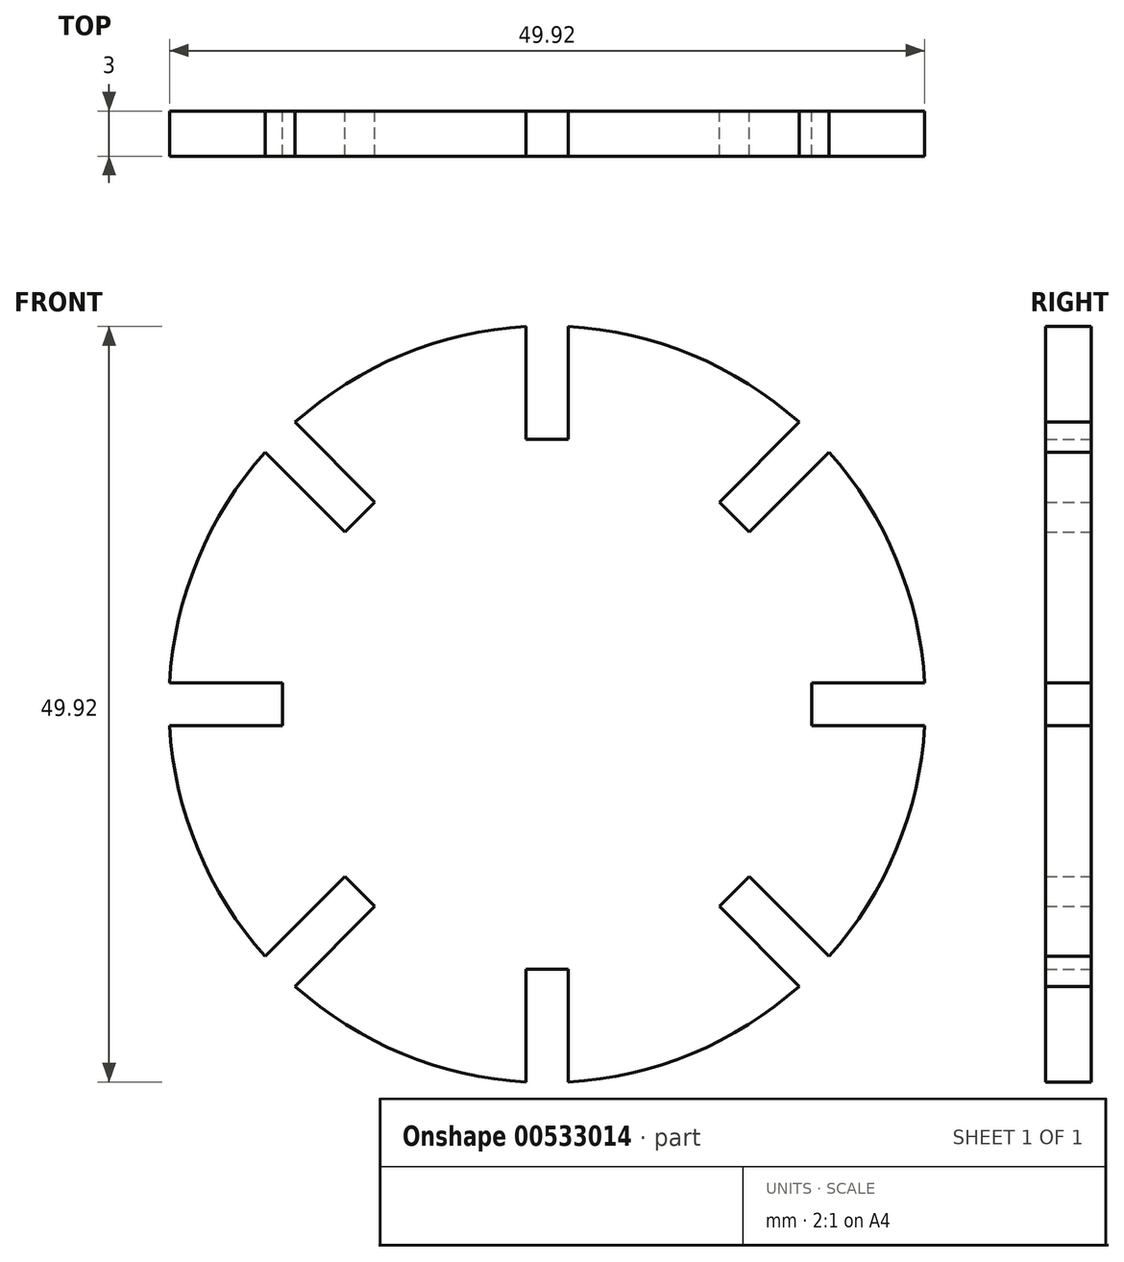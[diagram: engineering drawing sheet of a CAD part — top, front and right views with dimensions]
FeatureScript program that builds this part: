
annotation { "Feature Type Name" : "Feature", "Feature Type Description" : "" }
export const myFeature = defineFeature(function(context is Context, id is Id, definition is map)
    precondition{}
    {
        {
            var Q0;
            Q0=qCreatedBy(makeId("Front.planeOp"),FACE);
            var sketch = newSketch(context, id + "F0", { "sketchPlane" : qUnion([Q0])});
            skArc(sketch, "E0", {"start": v(16.66, 18.64) * mm, "mid": v(9.57, 23.1) * mm, "end": v(1.4, 24.96) * mm});
            skLineSegment(sketch, "E1.bottom", {"start": v(-1.4, 17.5) * mm, "end": v(1.4, 17.5) * mm});
            skLineSegment(sketch, "E1.left", {"start": v(-1.4, 17.5) * mm, "end": v(-1.4, 24.96) * mm});
            skLineSegment(sketch, "E1.right", {"start": v(1.4, 17.5) * mm, "end": v(1.4, 24.96) * mm});
            skPoint(sketch, "E1.middle", {"position": v(0, 25) * mm});
            skLineSegment(sketch, "E2.1.1", {"start": v(-11.38, 13.36) * mm, "end": v(-16.66, 18.64) * mm});
            skLineSegment(sketch, "E2.1.2", {"start": v(-13.36, 11.38) * mm, "end": v(-18.64, 16.66) * mm});
            skLineSegment(sketch, "E2.1.3", {"start": v(-13.36, 11.38) * mm, "end": v(-11.38, 13.36) * mm});
            skLineSegment(sketch, "E2.2.1", {"start": v(-17.5, 1.4) * mm, "end": v(-24.96, 1.4) * mm});
            skLineSegment(sketch, "E2.2.2", {"start": v(-17.5, -1.4) * mm, "end": v(-24.96, -1.4) * mm});
            skLineSegment(sketch, "E2.2.3", {"start": v(-17.5, -1.4) * mm, "end": v(-17.5, 1.4) * mm});
            skLineSegment(sketch, "E2.3.1", {"start": v(-13.36, -11.38) * mm, "end": v(-18.64, -16.66) * mm});
            skLineSegment(sketch, "E2.3.2", {"start": v(-11.38, -13.36) * mm, "end": v(-16.66, -18.64) * mm});
            skLineSegment(sketch, "E2.3.3", {"start": v(-11.38, -13.36) * mm, "end": v(-13.36, -11.38) * mm});
            skLineSegment(sketch, "E2.4.1", {"start": v(-1.4, -17.5) * mm, "end": v(-1.4, -24.96) * mm});
            skLineSegment(sketch, "E2.4.2", {"start": v(1.4, -17.5) * mm, "end": v(1.4, -24.96) * mm});
            skLineSegment(sketch, "E2.4.3", {"start": v(1.4, -17.5) * mm, "end": v(-1.4, -17.5) * mm});
            skLineSegment(sketch, "E2.5.1", {"start": v(11.38, -13.36) * mm, "end": v(16.66, -18.64) * mm});
            skLineSegment(sketch, "E2.5.2", {"start": v(13.36, -11.38) * mm, "end": v(18.64, -16.66) * mm});
            skLineSegment(sketch, "E2.5.3", {"start": v(13.36, -11.38) * mm, "end": v(11.38, -13.36) * mm});
            skLineSegment(sketch, "E2.6.1", {"start": v(17.5, -1.4) * mm, "end": v(24.96, -1.4) * mm});
            skLineSegment(sketch, "E2.6.2", {"start": v(17.5, 1.4) * mm, "end": v(24.96, 1.4) * mm});
            skLineSegment(sketch, "E2.6.3", {"start": v(17.5, 1.4) * mm, "end": v(17.5, -1.4) * mm});
            skLineSegment(sketch, "E2.7.1", {"start": v(13.36, 11.38) * mm, "end": v(18.64, 16.66) * mm});
            skLineSegment(sketch, "E2.7.2", {"start": v(11.38, 13.36) * mm, "end": v(16.66, 18.64) * mm});
            skLineSegment(sketch, "E2.7.3", {"start": v(11.38, 13.36) * mm, "end": v(13.36, 11.38) * mm});
            skPoint(sketch, "E3.orphan", {"position": v(23.97, 22) * mm});
            skPoint(sketch, "E4.orphan", {"position": v(22, 23.97) * mm});
            skArc(sketch, "E5.trimOffspring", {"start": v(-1.4, 24.96) * mm, "mid": v(-9.57, 23.1) * mm, "end": v(-16.66, 18.64) * mm});
            skPoint(sketch, "E1.top.end.orphan", {"position": v(1.4, 32.5) * mm});
            skPoint(sketch, "E6.orphan", {"position": v(-1.4, 32.5) * mm});
            skArc(sketch, "E7.trimOffspring", {"start": v(-18.64, 16.66) * mm, "mid": v(-23.1, 9.57) * mm, "end": v(-24.96, 1.4) * mm});
            skPoint(sketch, "E8.orphan", {"position": v(-23.97, 22) * mm});
            skPoint(sketch, "E9.orphan", {"position": v(-22, 23.97) * mm});
            skArc(sketch, "E10.trimOffspring", {"start": v(24.96, 1.4) * mm, "mid": v(23.1, 9.57) * mm, "end": v(18.64, 16.66) * mm});
            skPoint(sketch, "E11.orphan", {"position": v(-32.5, 1.4) * mm});
            skPoint(sketch, "E12.orphan", {"position": v(-32.5, -1.4) * mm});
            skArc(sketch, "E13.trimOffspring", {"start": v(-24.96, -1.4) * mm, "mid": v(-23.1, -9.57) * mm, "end": v(-18.64, -16.66) * mm});
            skArc(sketch, "E14.trimOffspring", {"start": v(-16.66, -18.64) * mm, "mid": v(-9.57, -23.1) * mm, "end": v(-1.4, -24.96) * mm});
            skArc(sketch, "E15.trimOffspring", {"start": v(1.4, -24.96) * mm, "mid": v(9.57, -23.1) * mm, "end": v(16.66, -18.64) * mm});
            skPoint(sketch, "E16.orphan", {"position": v(22, -23.97) * mm});
            skArc(sketch, "E17.trimOffspring", {"start": v(18.64, -16.66) * mm, "mid": v(23.1, -9.57) * mm, "end": v(24.96, -1.4) * mm});
            skSolve(sketch);
        }
        {
            var Q0;
            Q0 = qSketchRegion(id + "F0", true);
            extrude(context, id + "F1", {"entities" : qUnion([Q0]), "depth" : 3 * mm, "offsetDistance" : 25 * mm});
        }
    });
